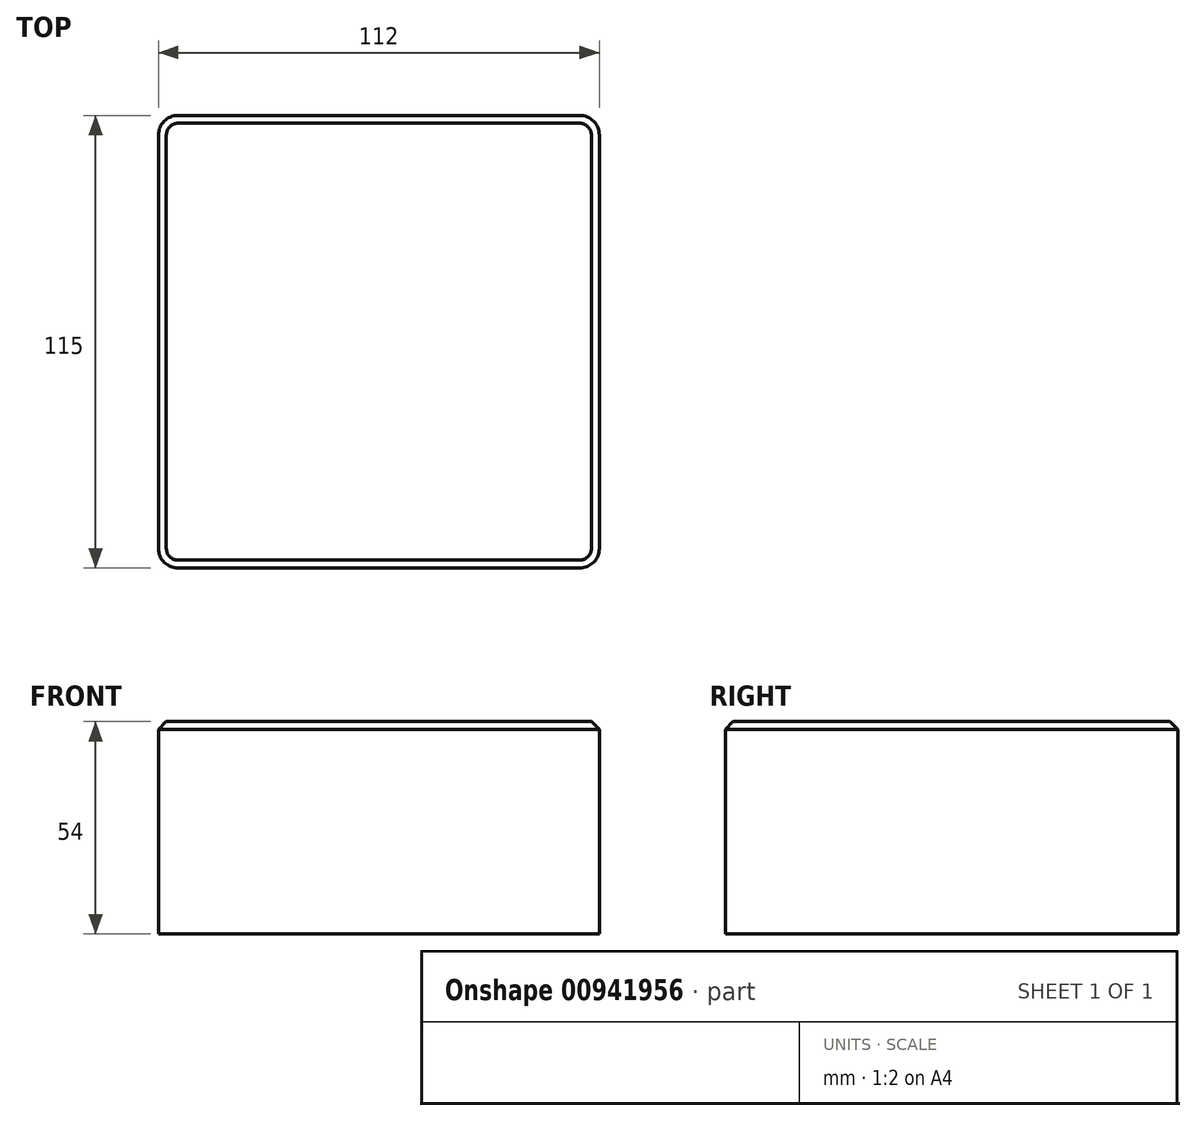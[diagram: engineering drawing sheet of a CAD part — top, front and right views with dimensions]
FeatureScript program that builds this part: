
annotation { "Feature Type Name" : "Feature", "Feature Type Description" : "" }
export const myFeature = defineFeature(function(context is Context, id is Id, definition is map)
    precondition{}
    {
        {
            var Q0;
            Q0=qCreatedBy(makeId("Top.planeOp"),FACE);
            var sketch = newSketch(context, id + "F0", { "sketchPlane" : qUnion([Q0])});
            skLineSegment(sketch, "E0.bottom", {"start": v(56, 57.5) * mm, "end": v(-56, 57.5) * mm});
            skLineSegment(sketch, "E0.top", {"start": v(56, -57.5) * mm, "end": v(-56, -57.5) * mm});
            skLineSegment(sketch, "E0.left", {"start": v(56, 57.5) * mm, "end": v(56, -57.5) * mm});
            skLineSegment(sketch, "E0.right", {"start": v(-56, 57.5) * mm, "end": v(-56, -57.5) * mm});
            skPoint(sketch, "E0.middle", {"position": v(0, 0) * mm});
            skSolve(sketch);
        }
        {
            var Q0;
            Q0=makeQuery(id+"F0.imprint","IMPRINT",FACE,{"disambiguationData":[TD([[makeQuery(id+"F0.imprint","IMPRINT",EDGE,{"derivedFrom":sQuery(id+"F0.wireOp",EDGE,"E0.bottom")}),1.0]])]});
            extrude(context, id + "F1", {"entities" : qUnion([Q0]), "depth" : 54 * mm, "offsetDistance" : 25 * mm});
        }
        {
            var Q0;
            Q0=makeQuery(id+"F1.opExtrude","SWEPT_EDGE",EDGE,{"disambiguationData":[OSD([sQuery(id+"F0.wireOp",EDGE,"E0.bottom"),sQuery(id+"F0.wireOp",EDGE,"E0.left")])]});
            var Q1;
            Q1=makeQuery(id+"F1.opExtrude","SWEPT_EDGE",EDGE,{"disambiguationData":[OSD([sQuery(id+"F0.wireOp",EDGE,"E0.bottom"),sQuery(id+"F0.wireOp",EDGE,"E0.right")])]});
            var Q2;
            Q2=makeQuery(id+"F1.opExtrude","SWEPT_EDGE",EDGE,{"disambiguationData":[OSD([sQuery(id+"F0.wireOp",EDGE,"E0.top"),sQuery(id+"F0.wireOp",EDGE,"E0.right")])]});
            var Q3;
            Q3=makeQuery(id+"F1.opExtrude","SWEPT_EDGE",EDGE,{"disambiguationData":[OSD([sQuery(id+"F0.wireOp",EDGE,"E0.top"),sQuery(id+"F0.wireOp",EDGE,"E0.left")])]});
            fillet(context, id + "F2", {"entities" : qUnion([Q0, Q1, Q2, Q3]), "radius" : 5 * mm, "tangentPropagation" : true, "allowEdgeOverflow" : false});
        }
        {
            var Q0;
            Q0=makeQuery(id+"F1.opExtrude","CAP_FACE",FACE,{"disambiguationData":[OSD([sQuery(id+"F0.wireOp",EDGE,"E0.bottom"),sQuery(id+"F0.wireOp",EDGE,"E0.top"),sQuery(id+"F0.wireOp",EDGE,"E0.left"),sQuery(id+"F0.wireOp",EDGE,"E0.right")])],"isStart":false});
            chamfer(context, id + "F3", {"entities" : qUnion([Q0]), "width" : 2 * mm, "tangentPropagation" : true});
        }
    });
